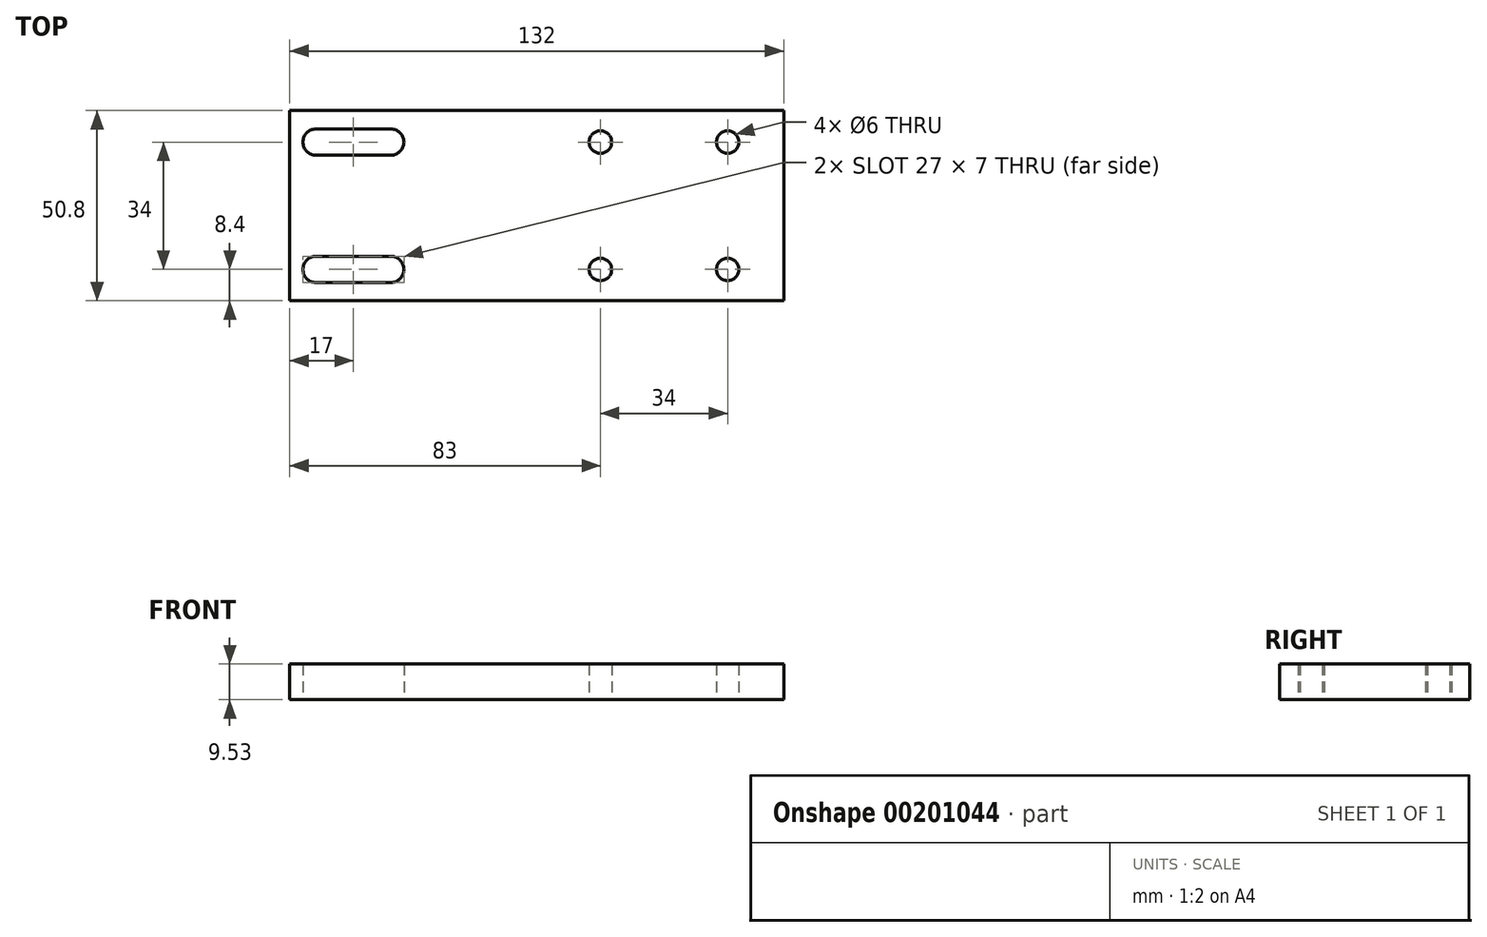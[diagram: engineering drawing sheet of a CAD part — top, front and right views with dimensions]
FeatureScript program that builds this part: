
annotation { "Feature Type Name" : "Feature", "Feature Type Description" : "" }
export const myFeature = defineFeature(function(context is Context, id is Id, definition is map)
    precondition{}
    {
        {
            var Q0;
            Q0=qCreatedBy(makeId("Top.planeOp"),FACE);
            var sketch = newSketch(context, id + "F0", { "sketchPlane" : qUnion([Q0])});
            skLineSegment(sketch, "E0.bottom", {"start": v(-66, 25.4) * mm, "end": v(66, 25.4) * mm});
            skLineSegment(sketch, "E0.top", {"start": v(-66, -25.4) * mm, "end": v(66, -25.4) * mm});
            skLineSegment(sketch, "E0.left", {"start": v(-66, 25.4) * mm, "end": v(-66, -25.4) * mm});
            skLineSegment(sketch, "E0.right", {"start": v(66, 25.4) * mm, "end": v(66, -25.4) * mm});
            skCircle(sketch, "E1", {"center": v(51, -17) * mm, "radius": 3 * mm});
            skCircle(sketch, "E2.MirrorC", {"center": v(51, 17) * mm, "radius": 3 * mm});
            skLineSegment(sketch, "E3", {"start": v(-59, 17) * mm, "end": v(-39, 17) * mm});
            skCircle(sketch, "E4", {"center": v(-39, 17) * mm, "radius": 3.5 * mm});
            skCircle(sketch, "E5", {"center": v(-59, 17) * mm, "radius": 3.5 * mm});
            skLineSegment(sketch, "E6", {"start": v(-59, 20.5) * mm, "end": v(-39, 20.5) * mm});
            skLineSegment(sketch, "E7", {"start": v(-39, 13.5) * mm, "end": v(-59, 13.5) * mm});
            skLineSegment(sketch, "E8.MirrorCS", {"start": v(-39, -13.5) * mm, "end": v(-59, -13.5) * mm});
            skLineSegment(sketch, "E9.MirrorCS", {"start": v(-59, -17) * mm, "end": v(-39, -17) * mm});
            skLineSegment(sketch, "E10.MirrorCS", {"start": v(-59, -20.5) * mm, "end": v(-39, -20.5) * mm});
            skCircle(sketch, "E11.MirrorC", {"center": v(-39, -17) * mm, "radius": 3.5 * mm});
            skCircle(sketch, "E12.MirrorC", {"center": v(-59, -17) * mm, "radius": 3.5 * mm});
            skLineSegment(sketch, "E13", {"start": v(34, -25.4) * mm, "end": v(34, 25.4) * mm});
            skCircle(sketch, "E14.MirrorC", {"center": v(17, 17) * mm, "radius": 3 * mm});
            skCircle(sketch, "E15.MirrorC", {"center": v(17, -17) * mm, "radius": 3 * mm});
            skSolve(sketch);
        }
        {
            var Q0;
            {var subQ6=sQuery(id+"F0.wireOp",EDGE,"E0.left");Q0=makeQuery(id+"F0.imprint","IMPRINT",FACE,{"disambiguationData":[TD([[makeQuery(id+"F0.imprint","IMPRINT",EDGE,{"derivedFrom":subQ6}),1.0]])]});}
            var Q1;
            {var subQ0=sQuery(id+"F0.wireOp",EDGE,"E0.right");Q1=makeQuery(id+"F0.imprint","IMPRINT",FACE,{"disambiguationData":[TD([[makeQuery(id+"F0.imprint","IMPRINT",EDGE,{"derivedFrom":subQ0}),-1.0]])]});}
            extrude(context, id + "F1", {"entities" : qUnion([Q0, Q1]), "depth" : 9.52 * mm});
        }
    });
